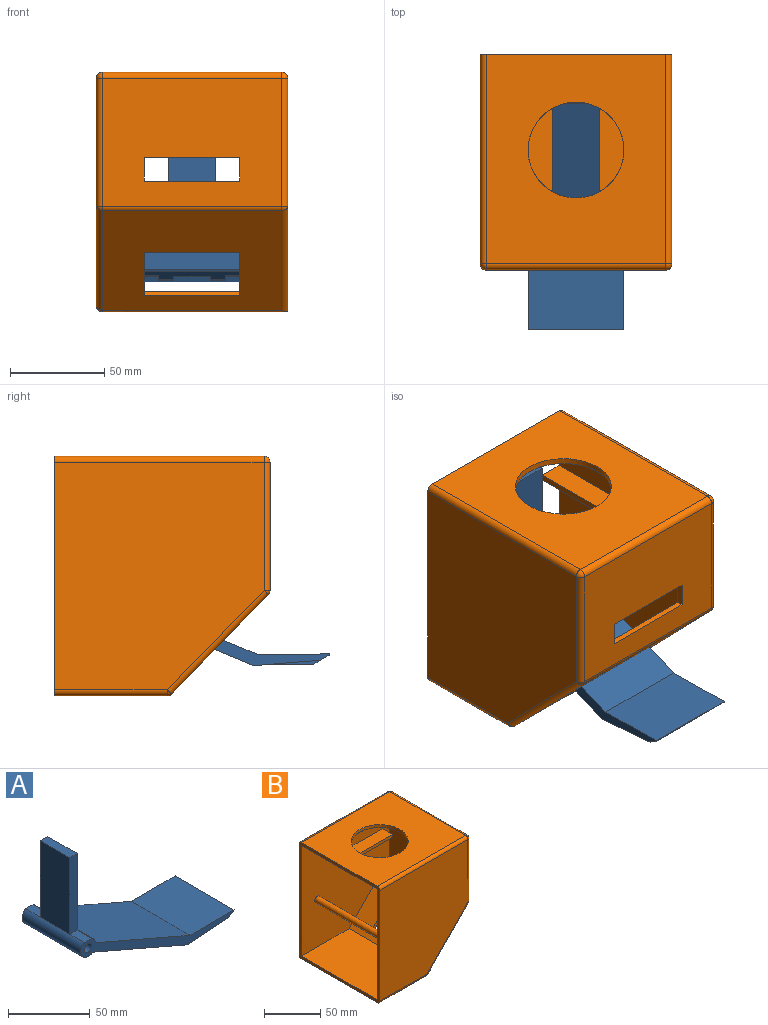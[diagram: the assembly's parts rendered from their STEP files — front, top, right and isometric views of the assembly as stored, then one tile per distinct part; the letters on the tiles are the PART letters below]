
ASSEMBLY  parts=2 mates=1
PART A: 28 faces, bbox 132.2x50.8x103 mm
  f0: plane 57.15x25.4mm, normal (-1,0,0), area 1451.6mm2, adj f1,f6,f24,f26
  f1: plane 25.4x6.35mm, normal (0,0,1), area 161.3mm2, adj f0,f4,f24,f26
  f2: plane 132.22x45.84mm, normal (0,-1,0), area 816mm2, adj f5,f6,f7,f8,f9,f10,f11,f12
  f3: plane 132.22x45.84mm, normal (0,1,0), area 816mm2, adj f5,f6,f7,f8,f9,f10,f11,f12
  f4: plane 57.15x25.4mm, normal (1,0,0), area 1451.6mm2, adj f1,f7,f24,f26
  f5: plane 50.8x7.51mm, normal (0.5,0,-0.87), area 308.5mm2, adj f2,f3,f12,f13,f15,f16,f18,f19
  f6: cylinder r=6.35mm len=50.8mm, axis (0,1,0), area 1051mm2, adj f0,f2,f3,f8,f25,f27
  f7: cylinder r=6.35mm len=50.8mm, axis (0,1,0), area 300.2mm2, adj f2,f3,f4,f11,f25,f27
  f8: plane 81.61x50.8mm, normal (-0.4,0,-0.92), area 4516.1mm2, adj f2,f3,f6,f12
  f9: plane 50.8x37.95mm, normal (0,0,1), area 1927.9mm2, adj f2,f3,f11,f23
  f10: cylinder r=3.17mm len=50.8mm, axis (0,1,0), area 1013.4mm2, adj f2,f3
  f11: plane 81.61x50.8mm, normal (0.4,0,0.92), area 4516.1mm2, adj f2,f3,f7,f9
  f12: plane 50.8x35.59mm, normal (0.07,0,-1), area 1305.2mm2, adj f2,f3,f5,f8,f13,f14,f15,f16
  f13: plane 30.99x2.54mm, normal (0,-1,0), area 28.9mm2, adj f5,f12,f14,f19,f22
  f14: plane 25.73x8.15mm, normal (0,0,-1), area 209.8mm2, adj f12,f13,f15,f19
  f15: plane 30.36x2.18mm, normal (0,1,0), area 28.9mm2, adj f5,f12,f14,f19
  f16: plane 30.36x2.18mm, normal (0,-1,0), area 28.9mm2, adj f5,f12,f17,f20
  f17: plane 25.73x8.15mm, normal (0,0,-1), area 209.8mm2, adj f12,f16,f18,f20
  f18: plane 30.99x2.54mm, normal (0,1,0), area 28.9mm2, adj f5,f12,f17,f20,f21
  f19: cylinder r=3.17mm len=8.15mm, axis (0,1,0), area 13.6mm2, adj f5,f13,f14,f15
  f20: cylinder r=3.17mm len=8.15mm, axis (0,-1,0), area 13.6mm2, adj f5,f16,f17,f18
  f21: cylinder r=3.17mm len=7.62mm, axis (0,-1,0), area 10.9mm2, adj f3,f5,f12,f18
  f22: cylinder r=3.17mm len=7.62mm, axis (0,-1,0), area 10.9mm2, adj f2,f5,f12,f13
  f23: cylinder r=0.8mm len=50.8mm, axis (0,-1,0), area 42.6mm2, adj f2,f3,f5,f9
  f24: plane 57.15x6.35mm, normal (0,-1,0), area 362.9mm2, adj f0,f1,f4,f25
  f25: plane 12.7x6.35mm, normal (0,0,1), area 80.6mm2, adj f2,f6,f7,f24
  f26: plane 57.15x6.35mm, normal (0,1,0), area 362.9mm2, adj f0,f1,f4,f27
  f27: plane 12.7x6.35mm, normal (0,0,1), area 80.6mm2, adj f3,f6,f7,f26
PART B: 52 faces, bbox 114.3x101.6x129.2 mm
  f0: plane 15.88x13.34mm, normal (-1,0,0), area 82.7mm2, adj f4,f46,f47,f48,f49,f51
  f1: plane 57.15x12.7mm, normal (0,0,1), area 725.8mm2, adj f42,f44,f45,f50
  f2: plane 57.15x15.88mm, normal (0,0,-1), area 907.3mm2, adj f42,f43,f44,f50
  f3: plane 15.88x13.34mm, normal (1,0,0), area 82.7mm2, adj f4,f46,f47,f48,f49,f51
  f4: plane 111.13x95.25mm, normal (0,0,-1), area 8194.9mm2, adj f0,f3,f8,f9,f15,f16,f32,f42
  f5: plane 95.25x52.76mm, normal (0.72,0,-0.7), area 5394.6mm2, adj f24,f27,f30,f31,f37,f38,f39,f40
  f6: plane 95.25x52.76mm, normal (-0.72,0,0.7), area 5394.6mm2, adj f8,f14,f15,f16,f37,f38,f39,f40
  f7: plane 95.25x67.89mm, normal (1,0,0), area 5821.3mm2, adj f19,f21,f24,f25,f33,f34,f35,f36
  f8: plane 95.25x67.89mm, normal (-1,0,0), area 5821.3mm2, adj f4,f6,f15,f16,f33,f34,f35,f36
  f9: plane 127x101.6mm, normal (-1,0,0), area 1404.8mm2, adj f4,f10,f11,f12,f13,f14,f15,f16
  f10: plane 98.43x59.85mm, normal (0,0,-1), area 5890.1mm2, adj f9,f13,f26,f30,f31
  f11: plane 111.13x95.25mm, normal (0,0,1), area 8557.8mm2, adj f9,f17,f19,f20,f32
  f12: plane 120.65x111.13mm, normal (0,-1,0), area 12054.7mm2, adj f9,f17,f21,f26,f27
  f13: plane 123.83x111.13mm, normal (0,1,0), area 12239.8mm2, adj f9,f10,f20,f25,f30
  f14: plane 95.25x59.85mm, normal (0,0,1), area 5701mm2, adj f6,f9,f15,f16
  f15: plane 120.65x111.13mm, normal (0,1,0), area 12023mm2, adj f4,f6,f8,f9,f14,f41
  f16: plane 120.65x111.13mm, normal (0,-1,0), area 12023mm2, adj f4,f6,f8,f9,f14,f41
  f17: cylinder r=3.17mm len=111.13mm, axis (1,0,0), area 554.2mm2, adj f9,f11,f12,f18
  f18: sphere r=3.17mm, area 15.8mm2, adj f17,f19,f21
  f19: cylinder r=3.17mm len=95.25mm, axis (0,1,0), area 475mm2, adj f7,f11,f18,f22
  f20: cylinder r=3.17mm len=111.13mm, axis (-1,0,0), area 554.2mm2, adj f9,f11,f13,f22
  f21: cylinder r=3.17mm len=67.89mm, axis (0,0,-1), area 338.6mm2, adj f7,f12,f18,f23
  f22: sphere r=3.17mm, area 15.8mm2, adj f19,f20,f25
  f23: sphere r=3.17mm, area 7.8mm2, adj f21,f24,f27
  f24: cylinder r=3.17mm len=95.25mm, axis (0,1,0), area 233.2mm2, adj f5,f7,f23,f28
  f25: cylinder r=3.17mm len=67.89mm, axis (0,0,1), area 338.6mm2, adj f7,f13,f22,f28
  f26: cylinder r=3.17mm len=59.85mm, axis (-1,0,0), area 298.5mm2, adj f9,f10,f12,f29
  f27: cylinder r=3.17mm len=54.97mm, axis (-0.7,0,-0.72), area 366.9mm2, adj f5,f12,f23,f29
  f28: sphere r=3.17mm, area 7.8mm2, adj f24,f25,f30
  f29: sphere r=3.17mm, area 8.1mm2, adj f26,f27,f31
  f30: cylinder r=3.17mm len=58.15mm, axis (0.7,0,0.72), area 378mm2, adj f5,f10,f13,f28,f31
  f31: cylinder r=3.17mm len=97.53mm, axis (0,1,0), area 244.9mm2, adj f5,f10,f29,f30
  f32: cylinder r=25.4mm len=50.8mm, axis (0,0,1), area 506.7mm2, adj f4,f11
  f33: plane 50.8x3.18mm, normal (0,0,-1), area 161.3mm2, adj f7,f8,f34,f36
  f34: plane 12.7x3.18mm, normal (0,1,0), area 40.3mm2, adj f7,f8,f33,f35
  f35: plane 50.8x3.18mm, normal (0,0,1), area 161.3mm2, adj f7,f8,f34,f36
  f36: plane 12.7x3.18mm, normal (0,-1,0), area 40.3mm2, adj f7,f8,f33,f35
  f37: plane 50.8x2.28mm, normal (-0.7,0,-0.72), area 161.3mm2, adj f5,f6,f38,f40
  f38: plane 24.98x24.4mm, normal (0,1,0), area 100.8mm2, adj f5,f6,f37,f39
  f39: plane 50.8x2.28mm, normal (0.7,0,0.72), area 161.3mm2, adj f5,f6,f38,f40
  f40: plane 24.98x24.4mm, normal (0,-1,0), area 100.8mm2, adj f5,f6,f37,f39
  f41: cylinder r=3.17mm len=95.25mm, axis (0,-1,0), area 1900.2mm2, adj f15,f16
  f42: plane 15.88x13.34mm, normal (-1,0,0), area 82.7mm2, adj f1,f2,f4,f43,f45,f50
  f43: plane 57.15x13.34mm, normal (0,1,0), area 762.1mm2, adj f2,f4,f42,f44
  f44: plane 15.88x13.34mm, normal (1,0,0), area 82.7mm2, adj f1,f2,f4,f43,f45,f50
  f45: plane 57.15x10.16mm, normal (0,-1,0), area 580.6mm2, adj f1,f4,f42,f44
  f46: plane 57.15x10.16mm, normal (0,1,0), area 580.6mm2, adj f0,f3,f4,f48
  f47: plane 57.15x13.34mm, normal (0,-1,0), area 762.1mm2, adj f0,f3,f4,f49
  f48: plane 57.15x12.7mm, normal (0,0,1), area 725.8mm2, adj f0,f3,f46,f51
  f49: plane 57.15x15.88mm, normal (0,0,-1), area 907.3mm2, adj f0,f3,f47,f51
  f50: plane 57.15x3.18mm, normal (0,-1,0), area 181.5mm2, adj f1,f2,f42,f44
  f51: plane 57.15x3.18mm, normal (0,1,0), area 181.5mm2, adj f0,f3,f48,f49
PLACE A rot(axis=(-0.01,-0.01,-1),90deg) t=(-25.4,-19.66,55.38)mm
PLACE B rot(axis=(0,0,-1),90deg) t=(0,0,0)mm
MATE revolute A.f10 <-> B.f41  axis (-1,0,0) through (-76.2,-19.66,55.38)mm
